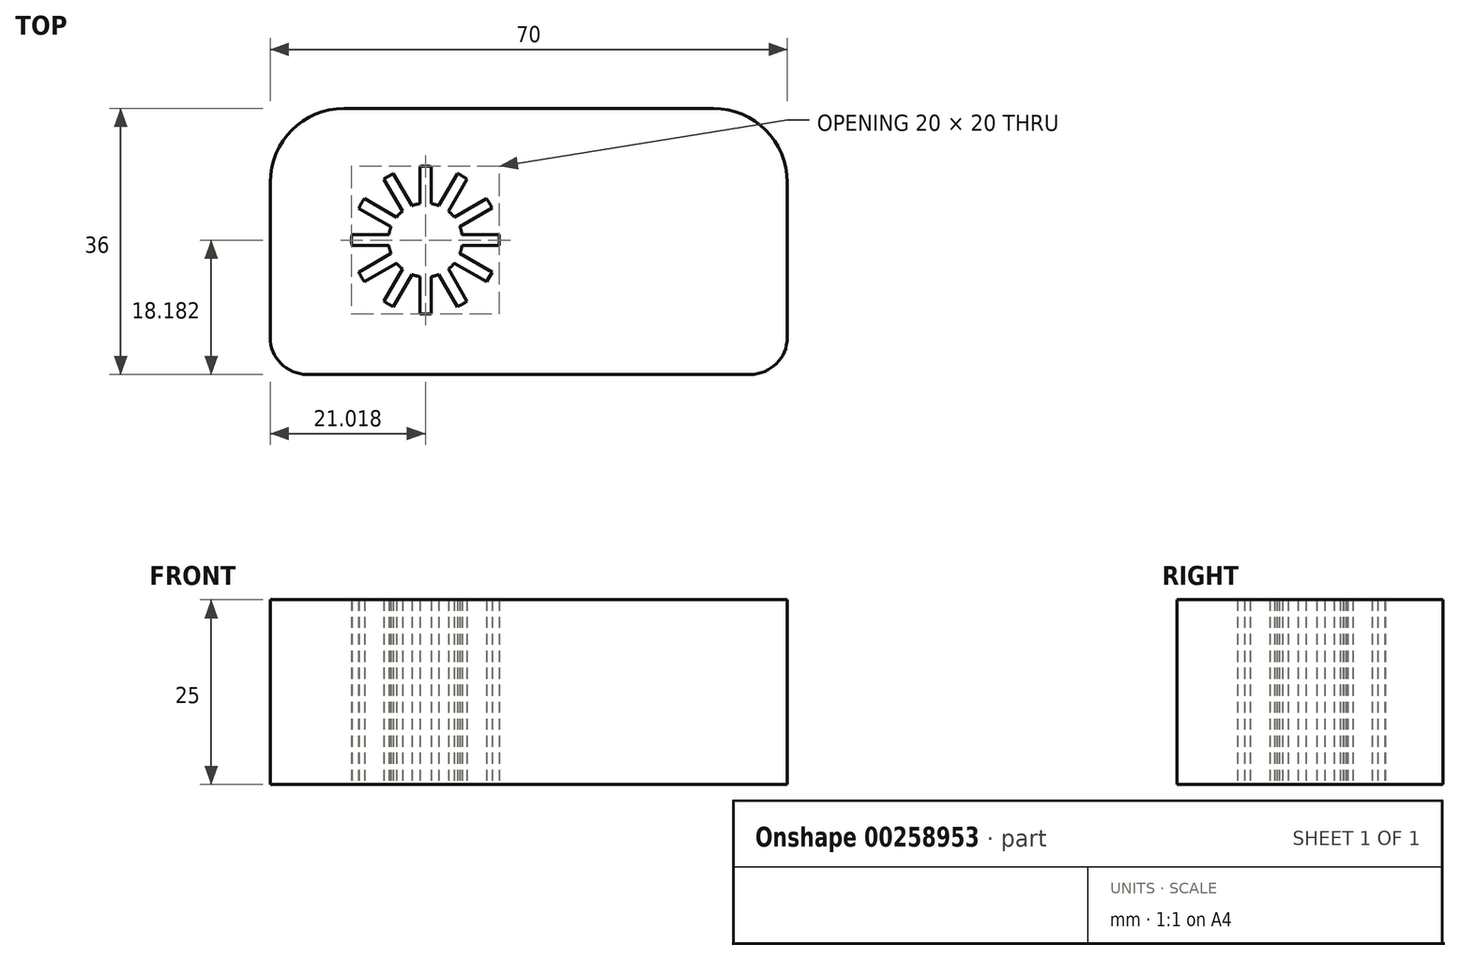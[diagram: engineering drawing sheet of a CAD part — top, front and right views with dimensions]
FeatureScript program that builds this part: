
annotation { "Feature Type Name" : "Feature", "Feature Type Description" : "" }
export const myFeature = defineFeature(function(context is Context, id is Id, definition is map)
    precondition{}
    {
        {
            var Q0;
            Q0=qCreatedBy(makeId("Top.planeOp"),FACE);
            var sketch = newSketch(context, id + "F0", { "sketchPlane" : qUnion([Q0])});
            skLineSegment(sketch, "E0", {"start": v(-30.28, -34.27) * mm, "end": v(29.72, -34.27) * mm});
            skLineSegment(sketch, "E1", {"start": v(34.72, -29.27) * mm, "end": v(34.72, -8.27) * mm});
            skLineSegment(sketch, "E2", {"start": v(24.72, 1.73) * mm, "end": v(-25.28, 1.73) * mm});
            skLineSegment(sketch, "E3", {"start": v(-35.28, -8.27) * mm, "end": v(-35.28, -29.27) * mm});
            skPoint(sketch, "E4.visualSharp", {"position": v(-35.28, 1.73) * mm});
            skArc(sketch, "E4.filletArc", {"start": v(-25.28, 1.73) * mm, "mid": v(-32.35, -1.2) * mm, "end": v(-35.28, -8.27) * mm});
            skPoint(sketch, "E5.visualSharp", {"position": v(34.72, -34.27) * mm});
            skArc(sketch, "E5.filletArc", {"start": v(29.72, -34.27) * mm, "mid": v(33.25, -32.8) * mm, "end": v(34.72, -29.27) * mm});
            skPoint(sketch, "E6.visualSharp", {"position": v(34.72, 1.73) * mm});
            skArc(sketch, "E6.filletArc", {"start": v(34.72, -8.27) * mm, "mid": v(31.79, -1.2) * mm, "end": v(24.72, 1.73) * mm});
            skPoint(sketch, "E7.visualSharp", {"position": v(-35.28, -34.27) * mm});
            skArc(sketch, "E7.filletArc", {"start": v(-35.28, -29.27) * mm, "mid": v(-33.82, -32.8) * mm, "end": v(-30.28, -34.27) * mm});
            skArc(sketch, "E8", {"start": v(-15.01, -11.14) * mm, "mid": v(-17.8, -12.55) * mm, "end": v(-19.2, -15.34) * mm});
            skArc(sketch, "E9", {"start": v(-18.6, -7.08) * mm, "mid": v(-19.26, -7.43) * mm, "end": v(-19.9, -7.83) * mm});
            skLineSegment(sketch, "E10", {"start": v(-4.29, -15.34) * mm, "end": v(-9.32, -15.34) * mm});
            skLineSegment(sketch, "E11", {"start": v(-4.29, -16.84) * mm, "end": v(-9.32, -16.84) * mm});
            skLineSegment(sketch, "E12.trimOffspring", {"start": v(-19.2, -15.34) * mm, "end": v(-24.23, -15.34) * mm});
            skLineSegment(sketch, "E13.trimOffspring", {"start": v(-19.2, -16.84) * mm, "end": v(-24.23, -16.84) * mm});
            skLineSegment(sketch, "E14", {"start": v(-13.51, -26.06) * mm, "end": v(-13.51, -21.03) * mm});
            skLineSegment(sketch, "E15", {"start": v(-15.01, -6.12) * mm, "end": v(-15.01, -11.14) * mm});
            skLineSegment(sketch, "E16.trimOffspring", {"start": v(-13.51, -11.14) * mm, "end": v(-13.51, -6.12) * mm});
            skLineSegment(sketch, "E17.trimOffspring", {"start": v(-15.01, -21.03) * mm, "end": v(-15.01, -26.06) * mm});
            skArc(sketch, "E18.trimOffspring", {"start": v(-9.32, -15.34) * mm, "mid": v(-10.73, -12.55) * mm, "end": v(-13.51, -11.14) * mm});
            skArc(sketch, "E19.trimOffspring", {"start": v(-13.51, -21.03) * mm, "mid": v(-10.73, -19.62) * mm, "end": v(-9.32, -16.84) * mm});
            skArc(sketch, "E20.trimOffspring", {"start": v(-19.2, -16.84) * mm, "mid": v(-17.8, -19.62) * mm, "end": v(-15.01, -21.03) * mm});
            skLineSegment(sketch, "E21", {"start": v(-19.9, -7.83) * mm, "end": v(-17.38, -12.18) * mm});
            skLineSegment(sketch, "E22", {"start": v(-18.6, -7.08) * mm, "end": v(-16.08, -11.43) * mm});
            skLineSegment(sketch, "E23", {"start": v(-12.44, -20.74) * mm, "end": v(-9.93, -25.1) * mm});
            skLineSegment(sketch, "E24", {"start": v(-11.14, -20) * mm, "end": v(-8.63, -24.35) * mm});
            skLineSegment(sketch, "E25", {"start": v(-22.52, -10.45) * mm, "end": v(-18.17, -12.97) * mm});
            skLineSegment(sketch, "E26", {"start": v(-18.92, -14.26) * mm, "end": v(-23.3, -11.8) * mm});
            skLineSegment(sketch, "E27", {"start": v(-9.6, -17.91) * mm, "end": v(-5.25, -20.42) * mm});
            skLineSegment(sketch, "E28", {"start": v(-10.36, -19.2) * mm, "end": v(-6, -21.72) * mm});
            skLineSegment(sketch, "E29", {"start": v(-18.92, -17.91) * mm, "end": v(-23.27, -20.42) * mm});
            skLineSegment(sketch, "E30", {"start": v(-18.17, -19.2) * mm, "end": v(-22.52, -21.72) * mm});
            skLineSegment(sketch, "E31", {"start": v(-17.38, -20) * mm, "end": v(-19.9, -24.35) * mm});
            skLineSegment(sketch, "E32", {"start": v(-16.08, -20.74) * mm, "end": v(-18.6, -25.1) * mm});
            skLineSegment(sketch, "E33", {"start": v(-9.92, -7.08) * mm, "end": v(-12.44, -11.43) * mm});
            skLineSegment(sketch, "E34", {"start": v(-9.26, -7.43) * mm, "end": v(-8.63, -7.83) * mm});
            skLineSegment(sketch, "E35", {"start": v(-8.63, -7.83) * mm, "end": v(-11.14, -12.18) * mm});
            skLineSegment(sketch, "E36", {"start": v(-10.36, -12.97) * mm, "end": v(-6, -10.45) * mm});
            skPoint(sketch, "E37.endSnap0", {"position": v(-9.93, -13.59) * mm});
            skLineSegment(sketch, "E38", {"start": v(-9.6, -14.27) * mm, "end": v(-5.25, -11.75) * mm});
            skPoint(sketch, "E39.orphan", {"position": v(-14.26, -6.09) * mm});
            skPoint(sketch, "E40.orphan", {"position": v(-5.6, -11.09) * mm});
            skPoint(sketch, "E41.orphan", {"position": v(-24.26, -16.09) * mm});
            skPoint(sketch, "E42.end.orphan", {"position": v(-4.29, -16.09) * mm});
            skArc(sketch, "E43.trimOffspring", {"start": v(-22.52, -10.45) * mm, "mid": v(-22.94, -11.11) * mm, "end": v(-23.3, -11.8) * mm});
            skArc(sketch, "E44.trimOffspring", {"start": v(-24.23, -15.34) * mm, "mid": v(-24.26, -16.09) * mm, "end": v(-24.23, -16.84) * mm});
            skArc(sketch, "E45.trimOffspring", {"start": v(-23.27, -20.42) * mm, "mid": v(-22.92, -21.09) * mm, "end": v(-22.52, -21.72) * mm});
            skArc(sketch, "E46.trimOffspring", {"start": v(-19.9, -24.35) * mm, "mid": v(-19.26, -24.75) * mm, "end": v(-18.6, -25.1) * mm});
            skArc(sketch, "E47.trimOffspring", {"start": v(-15.01, -26.06) * mm, "mid": v(-14.26, -26.09) * mm, "end": v(-13.51, -26.06) * mm});
            skArc(sketch, "E48.trimOffspring", {"start": v(-9.93, -25.1) * mm, "mid": v(-9.26, -24.75) * mm, "end": v(-8.63, -24.35) * mm});
            skArc(sketch, "E49.trimOffspring", {"start": v(-4.29, -16.84) * mm, "mid": v(-4.26, -16.09) * mm, "end": v(-4.29, -15.34) * mm});
            skArc(sketch, "E50.trimOffspring", {"start": v(-5.25, -11.75) * mm, "mid": v(-5.6, -11.09) * mm, "end": v(-6, -10.45) * mm});
            skArc(sketch, "E51.trimOffspring", {"start": v(-8.63, -7.83) * mm, "mid": v(-9.26, -7.43) * mm, "end": v(-9.92, -7.08) * mm});
            skArc(sketch, "E52.trimOffspring", {"start": v(-13.51, -6.12) * mm, "mid": v(-14.26, -6.09) * mm, "end": v(-15.01, -6.12) * mm});
            skLineSegment(sketch, "E53", {"start": v(-5.25, -20.42) * mm, "end": v(-6, -21.72) * mm});
            skSolve(sketch);
        }
        {
            var Q0;
            Q0 = qSketchRegion(id + "F0", true);
            var Q1;
            Q1=makeQuery(id+"F0.imprint","IMPRINT",FACE,{"disambiguationData":[TD([[makeQuery(id+"F0.imprint","IMPRINT",EDGE,{"derivedFrom":sQuery(id+"F0.wireOp",EDGE,"E0")}),1.0]])]});
            extrude(context, id + "F1", {"entities" : qUnion([Q0, Q1]), "depth" : 25 * mm});
        }
    });
